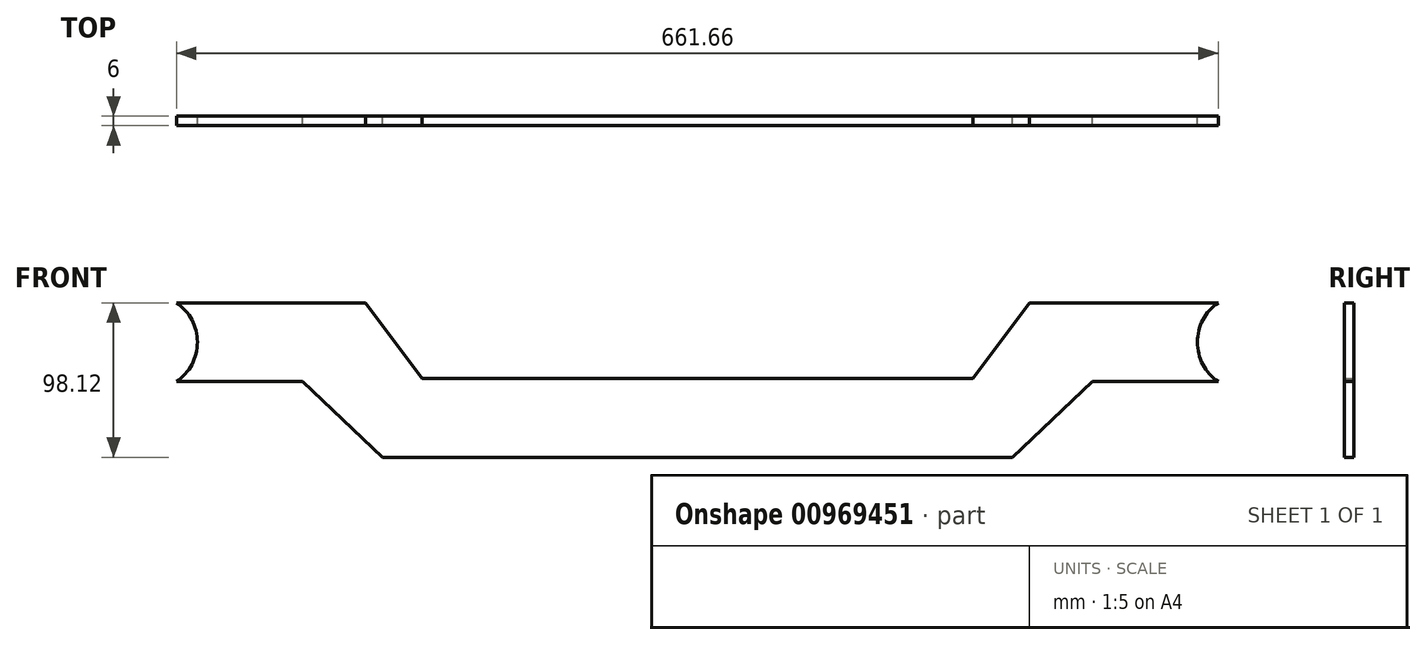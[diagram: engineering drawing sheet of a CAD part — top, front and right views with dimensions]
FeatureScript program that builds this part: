
annotation { "Feature Type Name" : "Feature", "Feature Type Description" : "" }
export const myFeature = defineFeature(function(context is Context, id is Id, definition is map)
    precondition{}
    {
        {
            var Q0;
            Q0=qCreatedBy(makeId("Front.planeOp"),FACE);
            var sketch = newSketch(context, id + "F0", { "sketchPlane" : qUnion([Q0])});
            skLineSegment(sketch, "E0", {"start": v(-200, 0) * mm, "end": v(200, 0) * mm});
            skLineSegment(sketch, "E1", {"start": v(-200, 0) * mm, "end": v(-250.83, 48.12) * mm});
            skLineSegment(sketch, "E2", {"start": v(-250.83, 48.12) * mm, "end": v(-330.83, 48.12) * mm});
            skLineSegment(sketch, "E3", {"start": v(-330.83, 98.12) * mm, "end": v(-210.83, 98.12) * mm});
            skLineSegment(sketch, "E4", {"start": v(-210.83, 98.12) * mm, "end": v(-175, 50) * mm});
            skLineSegment(sketch, "E5", {"start": v(-175, 50) * mm, "end": v(175, 50) * mm});
            skLineSegment(sketch, "E6", {"start": v(0, 0) * mm, "end": v(0, 122.25) * mm, "construction": true});
            skCircle(sketch, "E7", {"center": v(-347.69, 73.12) * mm, "radius": 30.15 * mm});
            skLineSegment(sketch, "E8.MirrorCS", {"start": v(210.83, 98.12) * mm, "end": v(175, 50) * mm});
            skLineSegment(sketch, "E9.MirrorCS", {"start": v(200, 0) * mm, "end": v(250.83, 48.12) * mm});
            skLineSegment(sketch, "E10.MirrorCS", {"start": v(250.83, 48.12) * mm, "end": v(330.83, 48.12) * mm});
            skLineSegment(sketch, "E11.MirrorCS", {"start": v(330.83, 98.12) * mm, "end": v(210.83, 98.12) * mm});
            skCircle(sketch, "E12.MirrorC", {"center": v(347.69, 73.12) * mm, "radius": 30.15 * mm});
            skSolve(sketch);
        }
        {
            var Q0;
            Q0=makeQuery(id+"F0.imprint","IMPRINT",FACE,{"disambiguationData":[TD([[makeQuery(id+"F0.imprint","IMPRINT",EDGE,{"derivedFrom":sQuery(id+"F0.wireOp",EDGE,"E0")}),1.0]])]});
            extrude(context, id + "F1", {"entities" : qUnion([Q0]), "depth" : 6 * mm, "offsetDistance" : 25 * mm});
        }
    });
